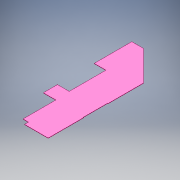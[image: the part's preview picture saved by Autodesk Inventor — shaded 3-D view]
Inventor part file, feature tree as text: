
AUTODESK INVENTOR PART (.ipt)
format: ipt  version: 2018 (Build 220112000, 112)  size: 126,464 bytes
history: native  units: mm
features: extrude x2, sketch x2
ambient origin geometry x8: Origin, YZ Plane, XZ Plane, XY Plane, X Axis, Y Axis, Z Axis, Center Point
bodies: Solid1 (feature_tree)
feature tree (4):
  extrude  "Extrusion1"  Depth=75.0mm
  extrude  "Extrusion2"  Depth=75.0mm
  sketch  "Sketch1"  dims[d0=240.0mm d1=75.0mm]
  sketch  "Sketch2"  dims[d4=235.0mm d5=75.0mm d6=90.0mm d7=80.0mm d8=210.0mm d9=35.0mm d10=25.0mm d12=1.6mm d13=0.0mm d16=75.0mm d17=270.0mm d18=45.0deg d19=3.0mm d20=155.0mm d21=225.0mm d22=10.0mm d23=0.0mm]
